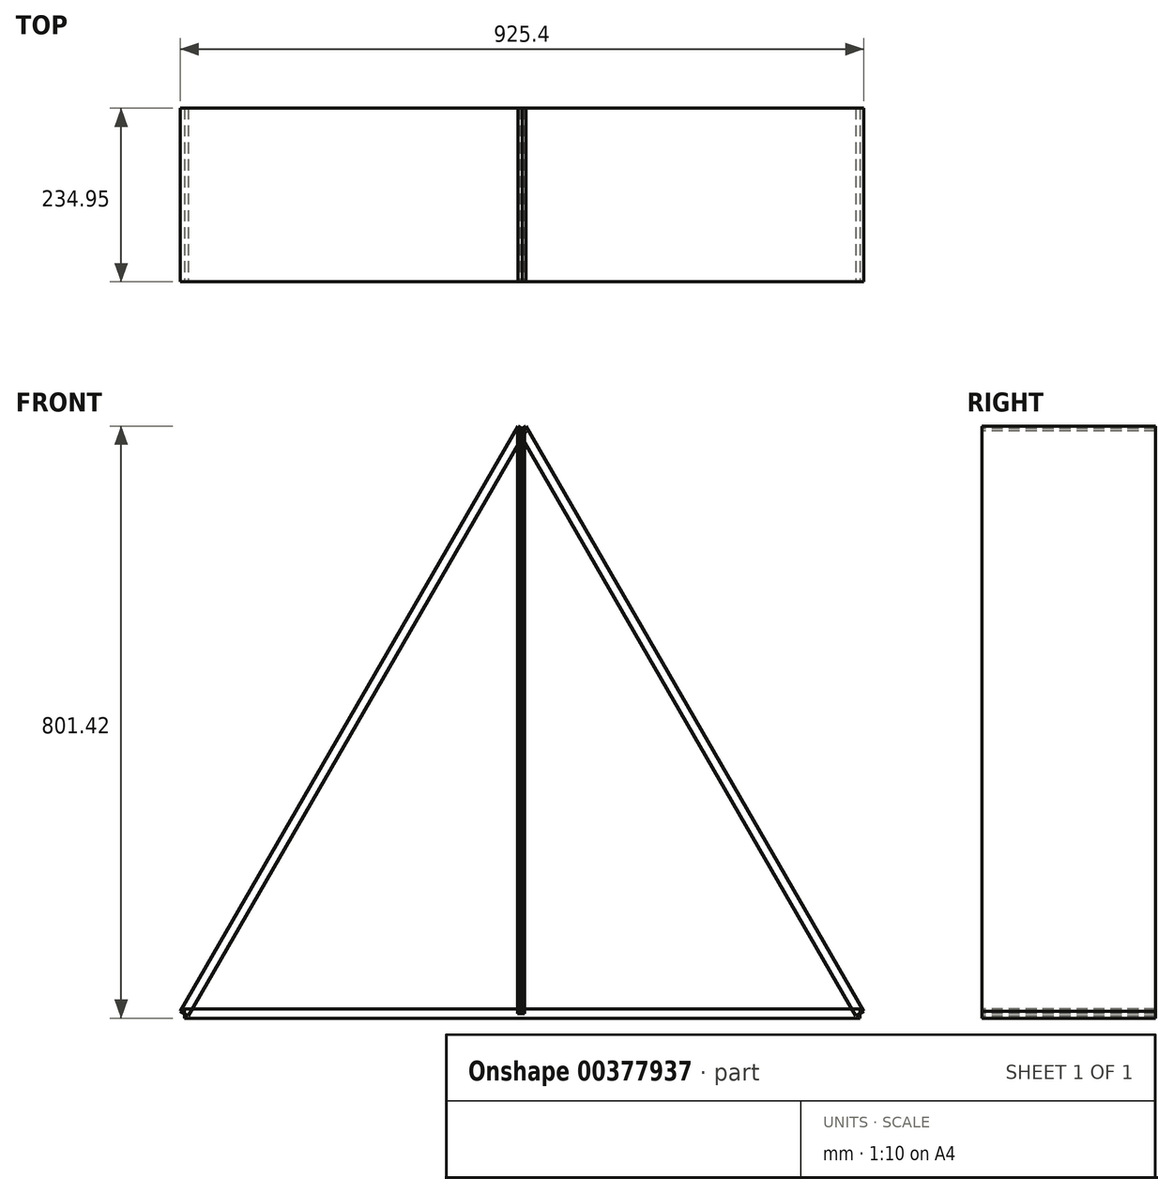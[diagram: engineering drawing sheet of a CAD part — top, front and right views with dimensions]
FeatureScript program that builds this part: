
annotation { "Feature Type Name" : "Feature", "Feature Type Description" : "" }
export const myFeature = defineFeature(function(context is Context, id is Id, definition is map)
    precondition{}
    {
        {
            var Q0;
            Q0=qCreatedBy(makeId("Front.planeOp"),FACE);
            var sketch = newSketch(context, id + "F0", { "sketchPlane" : qUnion([Q0])});
            skLineSegment(sketch, "E0", {"start": v(457.2, -84.72) * mm, "end": v(-457.2, -84.72) * mm});
            skLineSegment(sketch, "E1", {"start": v(0, -84.72) * mm, "end": v(0, 707.18) * mm});
            skLineSegment(sketch, "E2", {"start": v(0, 707.18) * mm, "end": v(-457.2, -84.72) * mm});
            skLineSegment(sketch, "E3", {"start": v(457.2, -84.72) * mm, "end": v(0, 707.18) * mm});
            skSolve(sketch);
        }
        {
            var Q0;
            Q0 = qSketchRegion(id + "F0", true);
            var Q1;
            Q1=sQuery(id+"F0.wireOp",EDGE,"E0");
            var Q2;
            Q2=sQuery(id+"F0.wireOp",EDGE,"E2");
            var Q3;
            Q3=sQuery(id+"F0.wireOp",EDGE,"E3");
            extrude(context, id + "F1", {"entities" : qUnion([Q0]), "bodyType" : ToolBodyType.SURFACE, "operationType" : NewBodyOperationType.INTERSECT, "surfaceEntities" : qUnion([Q1, Q2, Q3]), "depth" : 234.95 * mm});
        }
        {
            var Q0;
            Q0 = qSketchRegion(id + "F0", true);
            var Q1;
            Q1=sQuery(id+"F0.wireOp",EDGE,"E1");
            extrude(context, id + "F2", {"entities" : qUnion([Q0]), "bodyType" : ToolBodyType.SURFACE, "surfaceEntities" : qUnion([Q1]), "depth" : 234.95 * mm});
        }
        {
            var Q0;
            Q0=makeQuery(id+"F2.opExtrude","SWEPT_FACE",FACE,{"disambiguationData":[OSD([sQuery(id+"F0.wireOp",EDGE,"E1")])]});
            extrude(context, id + "F3", {"entities" : qUnion([Q0]), "endBound" : BoundingType.SYMMETRIC, "depth" : 6.35 * mm});
        }
        {
            var Q0;
            Q0=makeQuery(id+"F3.opExtrude","CAP_FACE",FACE,{"disambiguationData":[OSD([sQuery(id+"F0.wireOp",EDGE,"E1")])],"isStart":true});
            extrude(context, id + "F4", {"entities" : qUnion([Q0]), "endBound" : BoundingType.SYMMETRIC, "depth" : 6.35 * mm});
        }
        {
            var Q0;
            Q0=makeQuery(id+"F1.opExtrude","SWEPT_FACE",FACE,{"disambiguationData":[OSD([sQuery(id+"F0.wireOp",EDGE,"E0")])]});
            extrude(context, id + "F5", {"entities" : qUnion([Q0]), "endBound" : BoundingType.SYMMETRIC, "depth" : 12.7 * mm});
        }
        {
            var Q0;
            Q0=makeQuery(id+"F1.opExtrude","SWEPT_FACE",FACE,{"disambiguationData":[OSD([sQuery(id+"F0.wireOp",EDGE,"E3")])]});
            extrude(context, id + "F6", {"entities" : qUnion([Q0]), "endBound" : BoundingType.SYMMETRIC, "oppositeDirection" : true, "depth" : 12.7 * mm});
        }
        {
            var Q0;
            Q0=makeQuery(id+"F1.opExtrude","SWEPT_FACE",FACE,{"disambiguationData":[OSD([sQuery(id+"F0.wireOp",EDGE,"E2")])]});
            extrude(context, id + "F7", {"entities" : qUnion([Q0]), "endBound" : BoundingType.SYMMETRIC, "oppositeDirection" : true, "depth" : 12.7 * mm});
        }
        {
            var Q0;
            Q0=qCreatedBy(makeId("Front.planeOp"),FACE);
            var sketch = newSketch(context, id + "F8", { "sketchPlane" : qUnion([Q0])});
            skCircle(sketch, "E4", {"center": v(0, 177.96) * mm, "radius": 231.62 * mm});
            skSolve(sketch);
        }
        {
            var Q0;
            Q0 = qSketchRegion(id + "F8", true);
            var Q1;
            Q1=sQuery(id+"F8.wireOp",EDGE,"E4");
            extrude(context, id + "F9", {"entities" : qUnion([Q0]), "bodyType" : ToolBodyType.SURFACE, "surfaceEntities" : qUnion([Q1]), "depth" : 234.95 * mm});
        }
    });
